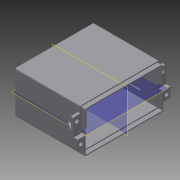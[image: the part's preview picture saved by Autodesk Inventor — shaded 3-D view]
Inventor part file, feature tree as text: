
AUTODESK INVENTOR PART (.ipt)
format: ipt  version: 2015 (Build 190159000, 159)  size: 320,000 bytes
history: native  units: in
note: dims shown in document units (in); Inventor stores cm internally (conversion verified against a paired STEP export)
features: sketch x13, extrude x11, fillet x4, mirror x4, plane x3, rib x2
ambient origin geometry x8: Origin, YZ Plane, XZ Plane, XY Plane, X Axis, Y Axis, Z Axis, Center Point
bodies: Solid1 (feature_tree)
feature tree (37):
  extrude  "Extrusion1"  Depth=1.9094in
  extrude  "Extrusion2"  Depth=2.2835in
  extrude  "Extrusion3"  Depth=0.0591in
  fillet  "Fillet1"  Radius=0.0591in
  extrude  "Extrusion4"  Depth=1.1024in TaperAngle=0.0deg
  plane  "Work Plane1"
  extrude  "Extrusion5"  Depth=0.0394in
  mirror  "Mirror1"
  extrude  "Extrusion6"  Depth=0.3937in
  fillet  "Fillet2"  Radius=0.5906in
  extrude  "Extrusion7"  Depth=0.0394in
  fillet  "Fillet3"  Radius=0.0394in
  extrude  "Extrusion8"  Depth=0.5906in
  extrude  "Extrusion9"  Depth=0.0394in TaperAngle=0.0deg
  fillet  "Fillet4"  Radius=0.0394in
  extrude  "Extrusion10"  Depth=0.315in
  extrude  "Extrusion11"  Depth=0.0787in TaperAngle=0.0deg
  mirror  "Mirror2"
  plane  "Work Plane2"
  rib  "Rib1"
  mirror  "Mirror3"
  plane  "Work Plane6"
  rib  "Rib3"
  mirror  "Mirror5"
  sketch  "Sketch1"  dims[d0=2.1654in d1=1.9094in]
  sketch  "Sketch2"  dims[d2=2.0276in d3=2.2835in]
  sketch  "Sketch3"  dims[d4=0.0591in d5=0.0591in d6=0.0591in d7=0.0in]
  sketch  "Sketch4"  dims[d8=2.1654in d9=1.1024in d10=0.0in]
  sketch  "Sketch5"  dims[d11=0.0591in d12=0.0in d13=0.0394in]
  sketch  "Sketch6"  dims[d14=0.1299in d15=0.3937in d16=0.5906in]
  sketch  "Sketch7"  dims[d17=0.3543in d18=0.0in d19=1.0827in d20=0.0394in]
  sketch  "Sketch8"  dims[d21=0.1772in d22=0.5906in]
  sketch  "Sketch9"  dims[d23=0.5906in d24=0.0394in d25=0.0in d26=0.0394in]
  sketch  "Sketch10"  dims[d27=0.9449in d28=0.315in]
  sketch  "Sketch11"  dims[d29=0.6693in d30=0.0787in d31=0.0in]
  sketch  "Sketch12"  dims[d32=0.0197in]
  sketch  "Sketch15"  dims[d33=0.0295in d34=0.0295in d35=0.0in d36=0.0295in d37=0.0in d38=0.0295in d39=0.0295in d40=0.6693in d41=0.0in d42=0.1181in d43=0.0in d44=0.0394in d45=2.2835in d46=0.6594in d47=0.0295in d48=0.0in d49=0.0295in d50=0.0295in d51=0.1181in d52=0.0in d60=0.0787in d61=0.502in d62=0.1969in d63=0.1969in d64=0.2854in d65=0.0in d66=0.1969in d67=0.0in d68=0.0394in d69=0.1181in d70=0.0984in d71=0.1378in d72=0.0787in d73=0.0in d74=0.1181in d75=0.1378in d76=0.0984in d77=0.1969in d78=0.0in d79=0.5512in d80=0.9963in d81=0.0394in d82=0.0787in d83=0.0in d84=0.0in d85=0.0394in d86=0.0394in d90=0.7874in d99=-0.0197in d100=0.0394in d101=135.0deg d102=0.0394in d103=0.0394in d104=0.0in d105=0.0in d106=0.0394in d107=0.0394in]
